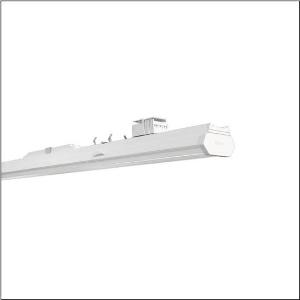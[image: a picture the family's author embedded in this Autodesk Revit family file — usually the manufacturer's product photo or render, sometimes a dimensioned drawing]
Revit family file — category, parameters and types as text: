
# Revit family: licross_r__11_protected_mo_51td12mn4axg_dbc1
name_source: partatom
category: Lighting Fixtures
units: mm (PartAtom-declared; Revit-internal decimal feet)

## family parameters
Cut with Voids When Loaded = No
Host = Face
Light Source = No
Part Type = Normal
Room Calculation Point = No
Round Connector Dimension = Use Diameter
Shared = No

## types (1)
- --- (1 x LED, 10020 lm, 55.3 W, 4000K)
    Apparent Load = 55 VA
    CIE Flux Codes = 73 92 98 99 100
    Color Rendering = 80
    Color Temperature = 4000K
    Default Elevation = 1800 mm
    Description = Licross® 11 Protected MO, luminaire insert, of sheet steel, galvanised, coil coated, white, length: 1.500mm, width: 90mm, height: 101mm, LED rated luminous flux: 10.030lm, light colour: 840, control gear: ON/OFF Multilumen, with plug, 3-pole, with phase selection, mains connection: 220..240V, AC, 50/60Hz, rated input power: 55W, halogen-free wiring, primary light control with lens, of plastic, primary optical cover: cover, of PMMA, light emission: direct distribution, primary light characteristic: symmetric, protection rating (complete): IP54, insulation class (complete): insulation class I (protective earthing), certification: CE, ENEC, VDE, UKCA, protection symbol: D if used in an environment with non-conductive dust loads with corresponding accessories, impact resistance: IK06, permissible ambient temperature for indoor applications: -35..+40°C, corresponds to IFS (International Featured Standards) requirements for safety and quality in the food industry, reducing of maximum allowable ambient temperature of 5°C with ceiling mounting, LABS conformity tested according to VDMA 24364:2018-05, packaging unit: 1 piece
    Height = 92 mm
    Lamp = 1 x LED
    Lamp Light Flux = 10020 lm
    Lamp Power = 55.3 W
    Lamp count = 1
    Length = 1500 mm
    Luminous efficacy = 181 lm/W
    Manufacturer = Siteco
    ModVariant = No
    Model = 51TD12MN4AXG
    Mounting Place = Ceiling
    Mounting Type = Pendant
    Number of Poles = 1
    OnlyDefault = Yes
    Power Factor = 1
    Product Name = Licross® 11 Protected MO
    Product group = luminaire insert
    ProductGroupID = 901
    Protection Class = Protection class I
    Protection Degree = IP 54
    RLX_Detail_Level = 1
    RLX_Emergency_Light_Flux = 0 lm
    RLX_Emergency_Type = 0
    RLX_Emergency_Type_DB = No
    RlxData = <blob elided: 22165 chars, md5=ecab0f7a>
    Socket = socket
    Standby Power = 0 W
    System Light Flux = 10020 lm
    System Power = 55 W
    Type Comments = factory setting: luminous flux: 100 % | (A | C | E) | 126 mA
    Type Image = l_1256145.jpg
    URL = http://relux.com
    VarID = @adj_055287
    Voltage = 0 V
    Weight = 0.00 kg
    Width = 88 mm

## geometry (parser evidence)
native form markers: Blend x4, Sweep x12
no freeform markers — native parametric forms only
